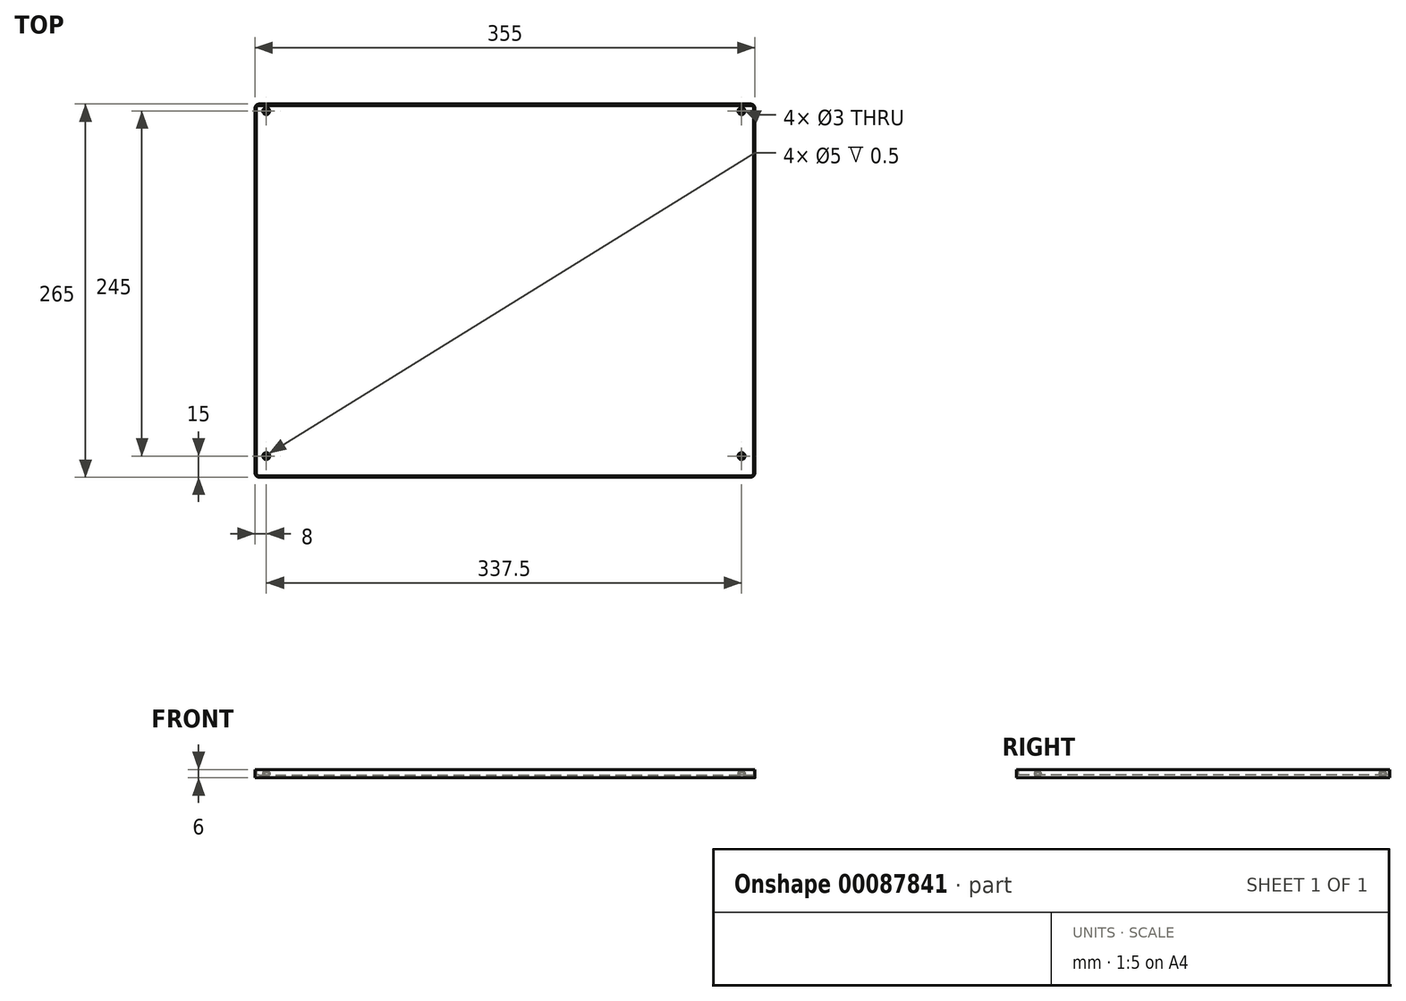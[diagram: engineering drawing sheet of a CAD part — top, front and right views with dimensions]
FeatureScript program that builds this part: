
annotation { "Feature Type Name" : "Feature", "Feature Type Description" : "" }
export const myFeature = defineFeature(function(context is Context, id is Id, definition is map)
    precondition{}
    {
        {
            var Q0;
            Q0=qCreatedBy(makeId("Top.planeOp"),FACE);
            var sketch = newSketch(context, id + "F0", { "sketchPlane" : qUnion([Q0])});
            skLineSegment(sketch, "E0.bottom", {"start": v(174.5, -132.5) * mm, "end": v(-174.5, -132.5) * mm});
            skLineSegment(sketch, "E0.top", {"start": v(174.5, 132.5) * mm, "end": v(-174.5, 132.5) * mm});
            skLineSegment(sketch, "E0.left", {"start": v(177.5, -129.5) * mm, "end": v(177.5, 129.5) * mm});
            skLineSegment(sketch, "E0.right", {"start": v(-177.5, -129.5) * mm, "end": v(-177.5, 129.5) * mm});
            skPoint(sketch, "E0.middle", {"position": v(0, 0) * mm});
            skPoint(sketch, "E1.visualSharp", {"position": v(-177.5, 132.5) * mm});
            skArc(sketch, "E1.filletArc", {"start": v(-174.5, 132.5) * mm, "mid": v(-176.62, 131.62) * mm, "end": v(-177.5, 129.5) * mm});
            skPoint(sketch, "E2.visualSharp", {"position": v(177.5, 132.5) * mm});
            skArc(sketch, "E2.filletArc", {"start": v(177.5, 129.5) * mm, "mid": v(176.62, 131.62) * mm, "end": v(174.5, 132.5) * mm});
            skPoint(sketch, "E3.visualSharp", {"position": v(177.5, -132.5) * mm});
            skArc(sketch, "E3.filletArc", {"start": v(174.5, -132.5) * mm, "mid": v(176.62, -131.62) * mm, "end": v(177.5, -129.5) * mm});
            skPoint(sketch, "E4.visualSharp", {"position": v(-177.5, -132.5) * mm});
            skArc(sketch, "E4.filletArc", {"start": v(-177.5, -129.5) * mm, "mid": v(-176.62, -131.62) * mm, "end": v(-174.5, -132.5) * mm});
            skSolve(sketch);
        }
        {
            var Q0;
            Q0=makeQuery(id+"F0.imprint","IMPRINT",FACE,{"disambiguationData":[TD([[makeQuery(id+"F0.imprint","IMPRINT",EDGE,{"derivedFrom":sQuery(id+"F0.wireOp",EDGE,"E0.bottom")}),-1.0]])]});
            extrude(context, id + "F1", {"entities" : qUnion([Q0]), "depth" : 2 * mm});
        }
        {
            var Q0;
            Q0=makeQuery(id+"F1.opExtrude","CAP_FACE",FACE,{"disambiguationData":[OSD([sQuery(id+"F0.wireOp",EDGE,"E0.bottom"),sQuery(id+"F0.wireOp",EDGE,"E0.top"),sQuery(id+"F0.wireOp",EDGE,"E0.left"),sQuery(id+"F0.wireOp",EDGE,"E0.right")])],"isStart":false});
            var sketch = newSketch(context, id + "F2", { "sketchPlane" : qUnion([Q0])});
            skCircle(sketch, "E5", {"center": v(-169.5, 127.5) * mm, "radius": 2.5 * mm});
            skCircle(sketch, "E6", {"center": v(-169.5, 127.5) * mm, "radius": 1.5 * mm});
            skCircle(sketch, "E7", {"center": v(168, 127.5) * mm, "radius": 2.5 * mm});
            skCircle(sketch, "E8", {"center": v(168, 127.5) * mm, "radius": 1.5 * mm});
            skCircle(sketch, "E9", {"center": v(-169.5, -117.5) * mm, "radius": 2.5 * mm});
            skCircle(sketch, "E10", {"center": v(-169.5, -117.5) * mm, "radius": 1.5 * mm});
            skCircle(sketch, "E11", {"center": v(168, -117.5) * mm, "radius": 2.5 * mm});
            skCircle(sketch, "E12", {"center": v(168, -117.5) * mm, "radius": 1.5 * mm});
            skSolve(sketch);
        }
        {
            var Q0;
            Q0 = qSketchRegion(id + "F2", true);
            extrude(context, id + "F3", {"entities" : qUnion([Q0]), "operationType" : NewBodyOperationType.ADD, "depth" : 2 * mm});
        }
        {
            var Q0;
            {var subQ0=sQuery(id+"F0.wireOp",EDGE,"E0.left");var subQ1=sQuery(id+"F0.wireOp",EDGE,"E4.filletArc");var subQ2=sQuery(id+"F0.wireOp",EDGE,"E3.filletArc");var subQ3=sQuery(id+"F0.wireOp",EDGE,"E2.filletArc");var subQ4=sQuery(id+"F0.wireOp",EDGE,"E1.filletArc");var subQ5=sQuery(id+"F0.wireOp",EDGE,"E0.bottom");var subQ6=sQuery(id+"F0.wireOp",EDGE,"E0.top");var subQ7=sQuery(id+"F0.wireOp",EDGE,"E0.right");Q0=makeQuery(id+"F3.boolean.opBoolean","SPLIT",FACE,{"disambiguationData":[TD([makeQuery(id+"F1.opExtrude","SWEPT_FACE",FACE,{"disambiguationData":[OSD([subQ5])]})])],"derivedFrom":makeQuery(id+"F1.opExtrude","CAP_FACE",FACE,{"disambiguationData":[OSD([subQ5,subQ6,subQ0,subQ7,subQ4,subQ3,subQ2,subQ1])],"isStart":false})});}
            var sketch = newSketch(context, id + "F4", { "sketchPlane" : qUnion([Q0])});
            skLineSegment(sketch, "E13.bottom", {"start": v(-174.5, 132.5) * mm, "end": v(174.5, 132.5) * mm});
            skLineSegment(sketch, "E13.top", {"start": v(-174.5, -132.5) * mm, "end": v(174.5, -132.5) * mm});
            skLineSegment(sketch, "E13.left", {"start": v(-177.5, 129.5) * mm, "end": v(-177.5, -129.5) * mm});
            skLineSegment(sketch, "E13.right", {"start": v(177.5, 129.5) * mm, "end": v(177.5, -129.5) * mm});
            skPoint(sketch, "E14.visualSharp", {"position": v(-177.5, 132.5) * mm});
            skArc(sketch, "E14.filletArc", {"start": v(-174.5, 132.5) * mm, "mid": v(-176.62, 131.62) * mm, "end": v(-177.5, 129.5) * mm});
            skPoint(sketch, "E15.visualSharp", {"position": v(177.5, 132.5) * mm});
            skArc(sketch, "E15.filletArc", {"start": v(177.5, 129.5) * mm, "mid": v(176.62, 131.62) * mm, "end": v(174.5, 132.5) * mm});
            skPoint(sketch, "E16.visualSharp", {"position": v(-177.5, -132.5) * mm});
            skArc(sketch, "E16.filletArc", {"start": v(-177.5, -129.5) * mm, "mid": v(-176.62, -131.62) * mm, "end": v(-174.5, -132.5) * mm});
            skPoint(sketch, "E17.visualSharp", {"position": v(177.5, -132.5) * mm});
            skArc(sketch, "E17.filletArc", {"start": v(174.5, -132.5) * mm, "mid": v(176.62, -131.62) * mm, "end": v(177.5, -129.5) * mm});
            skPoint(sketch, "E18.middle", {"position": v(0, 0) * mm});
            skArc(sketch, "E19.0", {"start": v(-174.5, 131.5) * mm, "mid": v(-175.91, 130.91) * mm, "end": v(-176.5, 129.5) * mm});
            skLineSegment(sketch, "E19.1", {"start": v(-174.5, 131.5) * mm, "end": v(174.5, 131.5) * mm});
            skLineSegment(sketch, "E19.2", {"start": v(-176.5, 129.5) * mm, "end": v(-176.5, -129.5) * mm});
            skArc(sketch, "E19.3", {"start": v(176.5, 129.5) * mm, "mid": v(175.91, 130.91) * mm, "end": v(174.5, 131.5) * mm});
            skArc(sketch, "E19.4", {"start": v(-176.5, -129.5) * mm, "mid": v(-175.91, -130.91) * mm, "end": v(-174.5, -131.5) * mm});
            skLineSegment(sketch, "E19.5", {"start": v(-174.5, -131.5) * mm, "end": v(174.5, -131.5) * mm});
            skArc(sketch, "E19.6", {"start": v(174.5, -131.5) * mm, "mid": v(175.91, -130.91) * mm, "end": v(176.5, -129.5) * mm});
            skLineSegment(sketch, "E19.7", {"start": v(176.5, 129.5) * mm, "end": v(176.5, -129.5) * mm});
            skSolve(sketch);
        }
        {
            var Q0;
            Q0 = qSketchRegion(id + "F4", true);
            extrude(context, id + "F5", {"entities" : qUnion([Q0]), "operationType" : NewBodyOperationType.ADD, "depth" : 4 * mm});
        }
        {
            var Q0;
            Q0=makeQuery(id+"F1.opExtrude","CAP_FACE",FACE,{"disambiguationData":[OSD([sQuery(id+"F0.wireOp",EDGE,"E0.bottom"),sQuery(id+"F0.wireOp",EDGE,"E0.top"),sQuery(id+"F0.wireOp",EDGE,"E0.left"),sQuery(id+"F0.wireOp",EDGE,"E0.right"),sQuery(id+"F0.wireOp",EDGE,"E1.filletArc"),sQuery(id+"F0.wireOp",EDGE,"E2.filletArc"),sQuery(id+"F0.wireOp",EDGE,"E3.filletArc"),sQuery(id+"F0.wireOp",EDGE,"E4.filletArc")])],"isStart":true});
            var sketch = newSketch(context, id + "F6", { "sketchPlane" : qUnion([Q0])});
            skPoint(sketch, "E20", {"position": v(-169.5, -127.5) * mm});
            skPoint(sketch, "E21", {"position": v(168, -127.5) * mm});
            skPoint(sketch, "E22", {"position": v(168, 117.5) * mm});
            skPoint(sketch, "E23", {"position": v(-169.5, 117.5) * mm});
            skSolve(sketch);
        }
        {
            var Q0;
            Q0=sQuery(id+"F6.wireOp",VERTEX,"E20");
            var Q1;
            Q1=sQuery(id+"F6.wireOp",VERTEX,"E21");
            var Q2;
            Q2=sQuery(id+"F6.wireOp",VERTEX,"E22");
            var Q3;
            Q3=sQuery(id+"F6.wireOp",VERTEX,"E23");
            var Q4;
            Q4=makeQuery(id+"F1.opExtrude","SWEPT_BODY",BODY,{"disambiguationData":[OSD([sQuery(id+"F0.wireOp",EDGE,"E0.bottom"),sQuery(id+"F0.wireOp",EDGE,"E0.top"),sQuery(id+"F0.wireOp",EDGE,"E0.left"),sQuery(id+"F0.wireOp",EDGE,"E0.right"),sQuery(id+"F0.wireOp",EDGE,"E1.filletArc"),sQuery(id+"F0.wireOp",EDGE,"E2.filletArc"),sQuery(id+"F0.wireOp",EDGE,"E3.filletArc"),sQuery(id+"F0.wireOp",EDGE,"E4.filletArc")])]});
            hole(context, id + "F7", {"style" : HoleStyle.C_BORE, "endStyle" : HoleEndStyle.THROUGH, "holeDiameter" : 3 * mm, "cBoreDiameter" : 5 * mm, "cBoreDepth" : 0.5 * mm, "locations" : qUnion([Q0, Q1, Q2, Q3]), "scope" : qUnion([Q4]), "isTappedThrough" : true});
        }
    });
